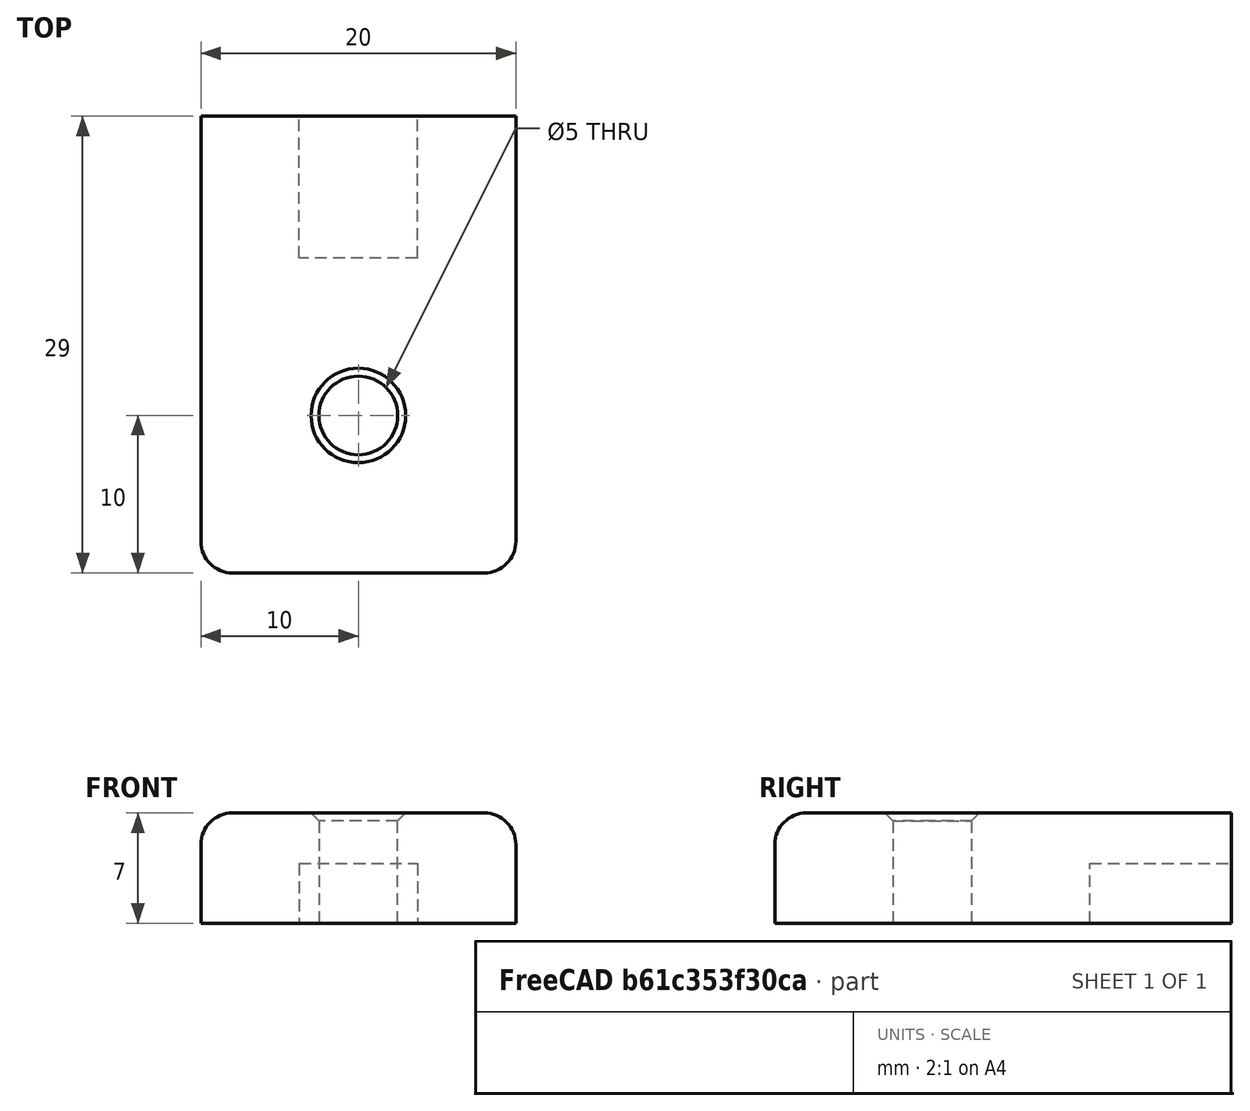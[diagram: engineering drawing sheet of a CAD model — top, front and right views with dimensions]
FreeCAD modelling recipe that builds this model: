
FCSTD DOCUMENT  (FreeCAD 0.20R29177 (Git))
Label: monturaHiwin
License: All rights reserved
LicenseURL: http://en.wikipedia.org/wiki/All_rights_reserved
objects: Part::Box×2, Part::Cut×2, Part::Fillet×2, Spreadsheet::Sheet×1, Part::Cylinder×1, Part::Chamfer×1
note: 8 computed .brp shape members not serialized (recipe doc carries the construction recipe); baked Part::Feature solids carry a one-line shape summary decoded from their .brp

FEATURE [Part::Box] Box  label="Riel"
  AttacherType = Attacher::AttachEngine3D
  Height = 4.8
  Length = 7.5
  Placement = pos=(-3.75,0,-1) rot=(0,0,1;0rad)
  Width = 20
  expr: .Placement.Base.x = -Spreadsheet.LonX_RielHiwinTOLmitad
  expr: .Placement.Base.z = -Spreadsheet.tolVer
  expr: Height = Spreadsheet.lonZ_RielHiwin
  expr: Length = Spreadsheet.lonX_RielHiwinTOL
FEATURE [Spreadsheet::Sheet] Spreadsheet
  cells = A1=variable; B1=Valor; A2=lonX_RielHiwin; B2(lonX_RielHiwin)=7; A3=lonZ_RielHiwin; B3(lonZ_RielHiwin)=4.8; A4=tol; B4(tol)=0.5; A5=lonX_RielHiwinTOL; B5(lonX_RielHiwinTOL)==B2 + B4; A6=lonZ_RielHiwinTOL; B6(lonZ_RielHiwinTOL)==B3 + B4; A7=lonX_RielHiwinTOLmitad; B7(LonX_RielHiwinTOLmitad)==B5 / 2; A8=tolVer; B8(tolVer)=1
FEATURE [Part::Box] Box001  label="Cubo001"
  AttacherType = Attacher::AttachEngine3D
  Height = 7
  Length = 20
  Placement = pos=(-10,-20,0) rot=(0,0,1;0rad)
  Width = 29
FEATURE [Part::Cylinder] Cylinder  label="Cilindro"
  Angle = 360
  AttacherType = Attacher::AttachEngine3D
  FirstAngle = 0
  Height = 20
  Placement = pos=(0,-10,-10) rot=(0,0,1;0rad)
  Radius = 2.5
  SecondAngle = 0
FEATURE [Part::Cut] Cut
  Base = -> Box001
  Tool = -> Box
FEATURE [Part::Cut] Cut001
  Base = -> Cut
  Tool = -> Cylinder
FEATURE [Part::Fillet] Fillet
  Base = -> Cut001
  Edges = 2 edges r=2: [Edge1,Edge6]
FEATURE [Part::Fillet] Fillet001
  Base = -> Fillet
  Edges = 1 edges r=2: [Edge1]
FEATURE [Part::Chamfer] Chamfer
  Base = -> Fillet001
  Edges = 1 edges r=0.5: [Edge32]
